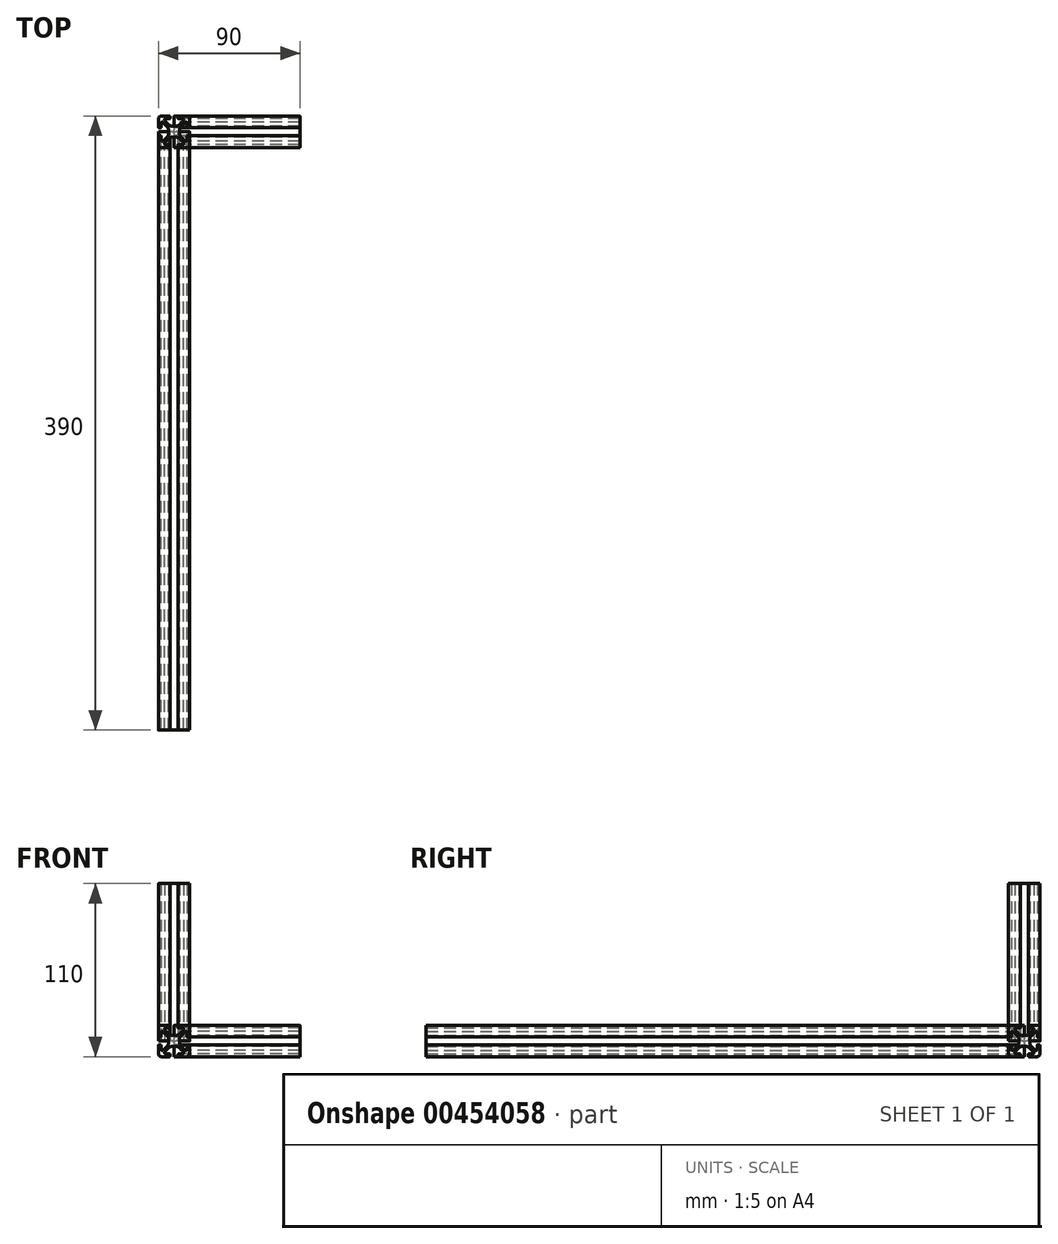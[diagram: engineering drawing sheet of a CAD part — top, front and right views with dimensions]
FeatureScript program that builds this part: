
annotation { "Feature Type Name" : "Feature", "Feature Type Description" : "" }
export const myFeature = defineFeature(function(context is Context, id is Id, definition is map)
    precondition{}
    {
        {
            var Q0;
            Q0=qCreatedBy(makeId("Top.planeOp"),FACE);
            var sketch = newSketch(context, id + "F0", { "sketchPlane" : qUnion([Q0])});
            skArc(sketch, "E0.0.0", {"start": v(-10, -8) * mm, "mid": v(-9.41, -9.41) * mm, "end": v(-8, -10) * mm});
            skLineSegment(sketch, "E0.0.1", {"start": v(-8, -10) * mm, "end": v(-3, -10) * mm});
            skArc(sketch, "E0.0.2", {"start": v(-3, -10) * mm, "mid": v(-2.65, -9.85) * mm, "end": v(-2.5, -9.5) * mm});
            skLineSegment(sketch, "E0.0.3", {"start": v(-2.5, -9.5) * mm, "end": v(-2.5, -8.4) * mm});
            skArc(sketch, "E0.0.4", {"start": v(-2.5, -8.4) * mm, "mid": v(-2.56, -8.26) * mm, "end": v(-2.7, -8.2) * mm});
            skLineSegment(sketch, "E0.0.5", {"start": v(-2.7, -8.2) * mm, "end": v(-5.34, -8.2) * mm});
            skArc(sketch, "E0.0.6", {"start": v(-5.34, -8.2) * mm, "mid": v(-6.04, -7.74) * mm, "end": v(-5.87, -6.92) * mm});
            skLineSegment(sketch, "E0.0.7", {"start": v(-5.87, -6.92) * mm, "end": v(-3.35, -4.4) * mm});
            skArc(sketch, "E0.0.8", {"start": v(-3.35, -4.4) * mm, "mid": v(-2.38, -3.75) * mm, "end": v(-1.23, -3.52) * mm});
            skLineSegment(sketch, "E0.0.9", {"start": v(-1.23, -3.52) * mm, "end": v(1.23, -3.52) * mm});
            skArc(sketch, "E0.0.10", {"start": v(1.23, -3.52) * mm, "mid": v(2.38, -3.75) * mm, "end": v(3.35, -4.4) * mm});
            skLineSegment(sketch, "E0.0.11", {"start": v(3.35, -4.4) * mm, "end": v(5.87, -6.92) * mm});
            skArc(sketch, "E0.0.12", {"start": v(5.87, -6.92) * mm, "mid": v(6.04, -7.74) * mm, "end": v(5.34, -8.2) * mm});
            skLineSegment(sketch, "E0.0.13", {"start": v(5.34, -8.2) * mm, "end": v(2.7, -8.2) * mm});
            skArc(sketch, "E0.0.14", {"start": v(2.7, -8.2) * mm, "mid": v(2.56, -8.26) * mm, "end": v(2.5, -8.4) * mm});
            skLineSegment(sketch, "E0.0.15", {"start": v(2.5, -8.4) * mm, "end": v(2.5, -9.5) * mm});
            skArc(sketch, "E0.0.16", {"start": v(2.5, -9.5) * mm, "mid": v(2.65, -9.85) * mm, "end": v(3, -10) * mm});
            skLineSegment(sketch, "E0.0.17", {"start": v(3, -10) * mm, "end": v(8, -10) * mm});
            skArc(sketch, "E0.0.18", {"start": v(8, -10) * mm, "mid": v(9.41, -9.41) * mm, "end": v(10, -8) * mm});
            skLineSegment(sketch, "E0.0.19", {"start": v(10, -8) * mm, "end": v(10, -3) * mm});
            skArc(sketch, "E0.0.20", {"start": v(10, -3) * mm, "mid": v(9.85, -2.65) * mm, "end": v(9.5, -2.5) * mm});
            skLineSegment(sketch, "E0.0.21", {"start": v(9.5, -2.5) * mm, "end": v(8.4, -2.5) * mm});
            skArc(sketch, "E0.0.22", {"start": v(8.4, -2.5) * mm, "mid": v(8.26, -2.56) * mm, "end": v(8.2, -2.7) * mm});
            skLineSegment(sketch, "E0.0.23", {"start": v(8.2, -2.7) * mm, "end": v(8.2, -5.34) * mm});
            skArc(sketch, "E0.0.24", {"start": v(8.2, -5.34) * mm, "mid": v(7.74, -6.04) * mm, "end": v(6.92, -5.87) * mm});
            skLineSegment(sketch, "E0.0.25", {"start": v(6.92, -5.87) * mm, "end": v(4.4, -3.35) * mm});
            skArc(sketch, "E0.0.26", {"start": v(4.4, -3.35) * mm, "mid": v(3.75, -2.38) * mm, "end": v(3.52, -1.23) * mm});
            skLineSegment(sketch, "E0.0.27", {"start": v(3.52, -1.23) * mm, "end": v(3.52, 1.23) * mm});
            skArc(sketch, "E0.0.28", {"start": v(3.52, 1.23) * mm, "mid": v(3.75, 2.38) * mm, "end": v(4.4, 3.35) * mm});
            skLineSegment(sketch, "E0.0.29", {"start": v(4.4, 3.35) * mm, "end": v(6.92, 5.87) * mm});
            skArc(sketch, "E0.0.30", {"start": v(6.92, 5.87) * mm, "mid": v(7.74, 6.04) * mm, "end": v(8.2, 5.34) * mm});
            skLineSegment(sketch, "E0.0.31", {"start": v(8.2, 5.34) * mm, "end": v(8.2, 2.7) * mm});
            skArc(sketch, "E0.0.32", {"start": v(8.2, 2.7) * mm, "mid": v(8.26, 2.56) * mm, "end": v(8.4, 2.5) * mm});
            skLineSegment(sketch, "E0.0.33", {"start": v(8.4, 2.5) * mm, "end": v(9.5, 2.5) * mm});
            skArc(sketch, "E0.0.34", {"start": v(9.5, 2.5) * mm, "mid": v(9.85, 2.65) * mm, "end": v(10, 3) * mm});
            skLineSegment(sketch, "E0.0.35", {"start": v(10, 3) * mm, "end": v(10, 8) * mm});
            skArc(sketch, "E0.0.36", {"start": v(10, 8) * mm, "mid": v(9.41, 9.41) * mm, "end": v(8, 10) * mm});
            skLineSegment(sketch, "E0.0.37", {"start": v(8, 10) * mm, "end": v(3, 10) * mm});
            skArc(sketch, "E0.0.38", {"start": v(3, 10) * mm, "mid": v(2.65, 9.85) * mm, "end": v(2.5, 9.5) * mm});
            skLineSegment(sketch, "E0.0.39", {"start": v(2.5, 9.5) * mm, "end": v(2.5, 8.4) * mm});
            skArc(sketch, "E0.0.40", {"start": v(2.5, 8.4) * mm, "mid": v(2.56, 8.26) * mm, "end": v(2.7, 8.2) * mm});
            skLineSegment(sketch, "E0.0.41", {"start": v(2.7, 8.2) * mm, "end": v(5.34, 8.2) * mm});
            skArc(sketch, "E0.0.42", {"start": v(5.34, 8.2) * mm, "mid": v(6.04, 7.74) * mm, "end": v(5.87, 6.92) * mm});
            skLineSegment(sketch, "E0.0.43", {"start": v(5.87, 6.92) * mm, "end": v(3.35, 4.4) * mm});
            skArc(sketch, "E0.0.44", {"start": v(3.35, 4.4) * mm, "mid": v(2.38, 3.75) * mm, "end": v(1.23, 3.52) * mm});
            skLineSegment(sketch, "E0.0.45", {"start": v(1.23, 3.52) * mm, "end": v(-1.23, 3.52) * mm});
            skArc(sketch, "E0.0.46", {"start": v(-1.23, 3.52) * mm, "mid": v(-2.38, 3.75) * mm, "end": v(-3.35, 4.4) * mm});
            skLineSegment(sketch, "E0.0.47", {"start": v(-3.35, 4.4) * mm, "end": v(-5.87, 6.92) * mm});
            skArc(sketch, "E0.0.48", {"start": v(-5.87, 6.92) * mm, "mid": v(-6.04, 7.74) * mm, "end": v(-5.34, 8.2) * mm});
            skLineSegment(sketch, "E0.0.49", {"start": v(-5.34, 8.2) * mm, "end": v(-2.7, 8.2) * mm});
            skArc(sketch, "E0.0.50", {"start": v(-2.7, 8.2) * mm, "mid": v(-2.56, 8.26) * mm, "end": v(-2.5, 8.4) * mm});
            skLineSegment(sketch, "E0.0.51", {"start": v(-2.5, 8.4) * mm, "end": v(-2.5, 9.5) * mm});
            skArc(sketch, "E0.0.52", {"start": v(-2.5, 9.5) * mm, "mid": v(-2.65, 9.85) * mm, "end": v(-3, 10) * mm});
            skLineSegment(sketch, "E0.0.53", {"start": v(-3, 10) * mm, "end": v(-8, 10) * mm});
            skArc(sketch, "E0.0.54", {"start": v(-8, 10) * mm, "mid": v(-9.41, 9.41) * mm, "end": v(-10, 8) * mm});
            skLineSegment(sketch, "E0.0.55", {"start": v(-10, 8) * mm, "end": v(-10, 3) * mm});
            skArc(sketch, "E0.0.56", {"start": v(-10, 3) * mm, "mid": v(-9.85, 2.65) * mm, "end": v(-9.5, 2.5) * mm});
            skLineSegment(sketch, "E0.0.57", {"start": v(-9.5, 2.5) * mm, "end": v(-8.4, 2.5) * mm});
            skArc(sketch, "E0.0.58", {"start": v(-8.4, 2.5) * mm, "mid": v(-8.26, 2.56) * mm, "end": v(-8.2, 2.7) * mm});
            skLineSegment(sketch, "E0.0.59", {"start": v(-8.2, 2.7) * mm, "end": v(-8.2, 5.34) * mm});
            skArc(sketch, "E0.0.60", {"start": v(-8.2, 5.34) * mm, "mid": v(-7.74, 6.04) * mm, "end": v(-6.92, 5.87) * mm});
            skLineSegment(sketch, "E0.0.61", {"start": v(-6.92, 5.87) * mm, "end": v(-4.4, 3.35) * mm});
            skArc(sketch, "E0.0.62", {"start": v(-4.4, 3.35) * mm, "mid": v(-3.75, 2.38) * mm, "end": v(-3.52, 1.23) * mm});
            skLineSegment(sketch, "E0.0.63", {"start": v(-3.52, 1.23) * mm, "end": v(-3.52, -1.23) * mm});
            skArc(sketch, "E0.0.64", {"start": v(-3.52, -1.23) * mm, "mid": v(-3.75, -2.38) * mm, "end": v(-4.4, -3.35) * mm});
            skLineSegment(sketch, "E0.0.65", {"start": v(-4.4, -3.35) * mm, "end": v(-6.92, -5.87) * mm});
            skArc(sketch, "E0.0.66", {"start": v(-6.92, -5.87) * mm, "mid": v(-7.74, -6.04) * mm, "end": v(-8.2, -5.34) * mm});
            skLineSegment(sketch, "E0.0.67", {"start": v(-8.2, -5.34) * mm, "end": v(-8.2, -2.7) * mm});
            skArc(sketch, "E0.0.68", {"start": v(-8.2, -2.7) * mm, "mid": v(-8.26, -2.56) * mm, "end": v(-8.4, -2.5) * mm});
            skLineSegment(sketch, "E0.0.69", {"start": v(-8.4, -2.5) * mm, "end": v(-9.5, -2.5) * mm});
            skArc(sketch, "E0.0.70", {"start": v(-9.5, -2.5) * mm, "mid": v(-9.85, -2.65) * mm, "end": v(-10, -3) * mm});
            skLineSegment(sketch, "E0.0.71", {"start": v(-10, -3) * mm, "end": v(-10, -8) * mm});
            skSolve(sketch);
        }
        {
            var Q0;
            Q0=qSketchRegion(id+"F0",true);
            extrude(context, id + "F1", {"entities" : qUnion([Q0]), "depth" : 100 * mm, "offsetDistance" : 25 * mm});
        }
        {
            var Q0;
            Q0=qCreatedBy(makeId("Right.planeOp"),FACE);
            var sketch = newSketch(context, id + "F2", { "sketchPlane" : qUnion([Q0])});
            skArc(sketch, "E1.0.0", {"start": v(-10, -8) * mm, "mid": v(-9.41, -9.41) * mm, "end": v(-8, -10) * mm});
            skLineSegment(sketch, "E1.0.1", {"start": v(-8, -10) * mm, "end": v(-3, -10) * mm});
            skArc(sketch, "E1.0.2", {"start": v(-3, -10) * mm, "mid": v(-2.65, -9.85) * mm, "end": v(-2.5, -9.5) * mm});
            skLineSegment(sketch, "E1.0.3", {"start": v(-2.5, -9.5) * mm, "end": v(-2.5, -8.4) * mm});
            skArc(sketch, "E1.0.4", {"start": v(-2.5, -8.4) * mm, "mid": v(-2.56, -8.26) * mm, "end": v(-2.7, -8.2) * mm});
            skLineSegment(sketch, "E1.0.5", {"start": v(-2.7, -8.2) * mm, "end": v(-5.34, -8.2) * mm});
            skArc(sketch, "E1.0.6", {"start": v(-5.34, -8.2) * mm, "mid": v(-6.04, -7.74) * mm, "end": v(-5.87, -6.92) * mm});
            skLineSegment(sketch, "E1.0.7", {"start": v(-5.87, -6.92) * mm, "end": v(-3.35, -4.4) * mm});
            skArc(sketch, "E1.0.8", {"start": v(-3.35, -4.4) * mm, "mid": v(-2.38, -3.75) * mm, "end": v(-1.23, -3.52) * mm});
            skLineSegment(sketch, "E1.0.9", {"start": v(-1.23, -3.52) * mm, "end": v(1.23, -3.52) * mm});
            skArc(sketch, "E1.0.10", {"start": v(1.23, -3.52) * mm, "mid": v(2.38, -3.75) * mm, "end": v(3.35, -4.4) * mm});
            skLineSegment(sketch, "E1.0.11", {"start": v(3.35, -4.4) * mm, "end": v(5.87, -6.92) * mm});
            skArc(sketch, "E1.0.12", {"start": v(5.87, -6.92) * mm, "mid": v(6.04, -7.74) * mm, "end": v(5.34, -8.2) * mm});
            skLineSegment(sketch, "E1.0.13", {"start": v(5.34, -8.2) * mm, "end": v(2.7, -8.2) * mm});
            skArc(sketch, "E1.0.14", {"start": v(2.7, -8.2) * mm, "mid": v(2.56, -8.26) * mm, "end": v(2.5, -8.4) * mm});
            skLineSegment(sketch, "E1.0.15", {"start": v(2.5, -8.4) * mm, "end": v(2.5, -9.5) * mm});
            skArc(sketch, "E1.0.16", {"start": v(2.5, -9.5) * mm, "mid": v(2.65, -9.85) * mm, "end": v(3, -10) * mm});
            skLineSegment(sketch, "E1.0.17", {"start": v(3, -10) * mm, "end": v(8, -10) * mm});
            skArc(sketch, "E1.0.18", {"start": v(8, -10) * mm, "mid": v(9.41, -9.41) * mm, "end": v(10, -8) * mm});
            skLineSegment(sketch, "E1.0.19", {"start": v(10, -8) * mm, "end": v(10, -3) * mm});
            skArc(sketch, "E1.0.20", {"start": v(10, -3) * mm, "mid": v(9.85, -2.65) * mm, "end": v(9.5, -2.5) * mm});
            skLineSegment(sketch, "E1.0.21", {"start": v(9.5, -2.5) * mm, "end": v(8.4, -2.5) * mm});
            skArc(sketch, "E1.0.22", {"start": v(8.4, -2.5) * mm, "mid": v(8.26, -2.56) * mm, "end": v(8.2, -2.7) * mm});
            skLineSegment(sketch, "E1.0.23", {"start": v(8.2, -2.7) * mm, "end": v(8.2, -5.34) * mm});
            skArc(sketch, "E1.0.24", {"start": v(8.2, -5.34) * mm, "mid": v(7.74, -6.04) * mm, "end": v(6.92, -5.87) * mm});
            skLineSegment(sketch, "E1.0.25", {"start": v(6.92, -5.87) * mm, "end": v(4.4, -3.35) * mm});
            skArc(sketch, "E1.0.26", {"start": v(4.4, -3.35) * mm, "mid": v(3.75, -2.38) * mm, "end": v(3.52, -1.23) * mm});
            skLineSegment(sketch, "E1.0.27", {"start": v(3.52, -1.23) * mm, "end": v(3.52, 1.23) * mm});
            skArc(sketch, "E1.0.28", {"start": v(3.52, 1.23) * mm, "mid": v(3.75, 2.38) * mm, "end": v(4.4, 3.35) * mm});
            skLineSegment(sketch, "E1.0.29", {"start": v(4.4, 3.35) * mm, "end": v(6.92, 5.87) * mm});
            skArc(sketch, "E1.0.30", {"start": v(6.92, 5.87) * mm, "mid": v(7.74, 6.04) * mm, "end": v(8.2, 5.34) * mm});
            skLineSegment(sketch, "E1.0.31", {"start": v(8.2, 5.34) * mm, "end": v(8.2, 2.7) * mm});
            skArc(sketch, "E1.0.32", {"start": v(8.2, 2.7) * mm, "mid": v(8.26, 2.56) * mm, "end": v(8.4, 2.5) * mm});
            skLineSegment(sketch, "E1.0.33", {"start": v(8.4, 2.5) * mm, "end": v(9.5, 2.5) * mm});
            skArc(sketch, "E1.0.34", {"start": v(9.5, 2.5) * mm, "mid": v(9.85, 2.65) * mm, "end": v(10, 3) * mm});
            skLineSegment(sketch, "E1.0.35", {"start": v(10, 3) * mm, "end": v(10, 8) * mm});
            skArc(sketch, "E1.0.36", {"start": v(10, 8) * mm, "mid": v(9.41, 9.41) * mm, "end": v(8, 10) * mm});
            skLineSegment(sketch, "E1.0.37", {"start": v(8, 10) * mm, "end": v(3, 10) * mm});
            skArc(sketch, "E1.0.38", {"start": v(3, 10) * mm, "mid": v(2.65, 9.85) * mm, "end": v(2.5, 9.5) * mm});
            skLineSegment(sketch, "E1.0.39", {"start": v(2.5, 9.5) * mm, "end": v(2.5, 8.4) * mm});
            skArc(sketch, "E1.0.40", {"start": v(2.5, 8.4) * mm, "mid": v(2.56, 8.26) * mm, "end": v(2.7, 8.2) * mm});
            skLineSegment(sketch, "E1.0.41", {"start": v(2.7, 8.2) * mm, "end": v(5.34, 8.2) * mm});
            skArc(sketch, "E1.0.42", {"start": v(5.34, 8.2) * mm, "mid": v(6.04, 7.74) * mm, "end": v(5.87, 6.92) * mm});
            skLineSegment(sketch, "E1.0.43", {"start": v(5.87, 6.92) * mm, "end": v(3.35, 4.4) * mm});
            skArc(sketch, "E1.0.44", {"start": v(3.35, 4.4) * mm, "mid": v(2.38, 3.75) * mm, "end": v(1.23, 3.52) * mm});
            skLineSegment(sketch, "E1.0.45", {"start": v(1.23, 3.52) * mm, "end": v(-1.23, 3.52) * mm});
            skArc(sketch, "E1.0.46", {"start": v(-1.23, 3.52) * mm, "mid": v(-2.38, 3.75) * mm, "end": v(-3.35, 4.4) * mm});
            skLineSegment(sketch, "E1.0.47", {"start": v(-3.35, 4.4) * mm, "end": v(-5.87, 6.92) * mm});
            skArc(sketch, "E1.0.48", {"start": v(-5.87, 6.92) * mm, "mid": v(-6.04, 7.74) * mm, "end": v(-5.34, 8.2) * mm});
            skLineSegment(sketch, "E1.0.49", {"start": v(-5.34, 8.2) * mm, "end": v(-2.7, 8.2) * mm});
            skArc(sketch, "E1.0.50", {"start": v(-2.7, 8.2) * mm, "mid": v(-2.56, 8.26) * mm, "end": v(-2.5, 8.4) * mm});
            skLineSegment(sketch, "E1.0.51", {"start": v(-2.5, 8.4) * mm, "end": v(-2.5, 9.5) * mm});
            skArc(sketch, "E1.0.52", {"start": v(-2.5, 9.5) * mm, "mid": v(-2.65, 9.85) * mm, "end": v(-3, 10) * mm});
            skLineSegment(sketch, "E1.0.53", {"start": v(-3, 10) * mm, "end": v(-8, 10) * mm});
            skArc(sketch, "E1.0.54", {"start": v(-8, 10) * mm, "mid": v(-9.41, 9.41) * mm, "end": v(-10, 8) * mm});
            skLineSegment(sketch, "E1.0.55", {"start": v(-10, 8) * mm, "end": v(-10, 3) * mm});
            skArc(sketch, "E1.0.56", {"start": v(-10, 3) * mm, "mid": v(-9.85, 2.65) * mm, "end": v(-9.5, 2.5) * mm});
            skLineSegment(sketch, "E1.0.57", {"start": v(-9.5, 2.5) * mm, "end": v(-8.4, 2.5) * mm});
            skArc(sketch, "E1.0.58", {"start": v(-8.4, 2.5) * mm, "mid": v(-8.26, 2.56) * mm, "end": v(-8.2, 2.7) * mm});
            skLineSegment(sketch, "E1.0.59", {"start": v(-8.2, 2.7) * mm, "end": v(-8.2, 5.34) * mm});
            skArc(sketch, "E1.0.60", {"start": v(-8.2, 5.34) * mm, "mid": v(-7.74, 6.04) * mm, "end": v(-6.92, 5.87) * mm});
            skLineSegment(sketch, "E1.0.61", {"start": v(-6.92, 5.87) * mm, "end": v(-4.4, 3.35) * mm});
            skArc(sketch, "E1.0.62", {"start": v(-4.4, 3.35) * mm, "mid": v(-3.75, 2.38) * mm, "end": v(-3.52, 1.23) * mm});
            skLineSegment(sketch, "E1.0.63", {"start": v(-3.52, 1.23) * mm, "end": v(-3.52, -1.23) * mm});
            skArc(sketch, "E1.0.64", {"start": v(-3.52, -1.23) * mm, "mid": v(-3.75, -2.38) * mm, "end": v(-4.4, -3.35) * mm});
            skLineSegment(sketch, "E1.0.65", {"start": v(-4.4, -3.35) * mm, "end": v(-6.92, -5.87) * mm});
            skArc(sketch, "E1.0.66", {"start": v(-6.92, -5.87) * mm, "mid": v(-7.74, -6.04) * mm, "end": v(-8.2, -5.34) * mm});
            skLineSegment(sketch, "E1.0.67", {"start": v(-8.2, -5.34) * mm, "end": v(-8.2, -2.7) * mm});
            skArc(sketch, "E1.0.68", {"start": v(-8.2, -2.7) * mm, "mid": v(-8.26, -2.56) * mm, "end": v(-8.4, -2.5) * mm});
            skLineSegment(sketch, "E1.0.69", {"start": v(-8.4, -2.5) * mm, "end": v(-9.5, -2.5) * mm});
            skArc(sketch, "E1.0.70", {"start": v(-9.5, -2.5) * mm, "mid": v(-9.85, -2.65) * mm, "end": v(-10, -3) * mm});
            skLineSegment(sketch, "E1.0.71", {"start": v(-10, -3) * mm, "end": v(-10, -8) * mm});
            skSolve(sketch);
        }
        {
            var Q0;
            Q0=qSketchRegion(id+"F2",true);
            extrude(context, id + "F3", {"entities" : qUnion([Q0]), "depth" : 80 * mm, "offsetDistance" : 25 * mm});
        }
        {
            var Q0;
            Q0=qCreatedBy(makeId("Front.planeOp"),FACE);
            var sketch = newSketch(context, id + "F4", { "sketchPlane" : qUnion([Q0])});
            skArc(sketch, "E2.0.0", {"start": v(-10, -8) * mm, "mid": v(-9.41, -9.41) * mm, "end": v(-8, -10) * mm});
            skLineSegment(sketch, "E2.0.1", {"start": v(-8, -10) * mm, "end": v(-3, -10) * mm});
            skArc(sketch, "E2.0.2", {"start": v(-3, -10) * mm, "mid": v(-2.65, -9.85) * mm, "end": v(-2.5, -9.5) * mm});
            skLineSegment(sketch, "E2.0.3", {"start": v(-2.5, -9.5) * mm, "end": v(-2.5, -8.4) * mm});
            skArc(sketch, "E2.0.4", {"start": v(-2.5, -8.4) * mm, "mid": v(-2.56, -8.26) * mm, "end": v(-2.7, -8.2) * mm});
            skLineSegment(sketch, "E2.0.5", {"start": v(-2.7, -8.2) * mm, "end": v(-5.34, -8.2) * mm});
            skArc(sketch, "E2.0.6", {"start": v(-5.34, -8.2) * mm, "mid": v(-6.04, -7.74) * mm, "end": v(-5.87, -6.92) * mm});
            skLineSegment(sketch, "E2.0.7", {"start": v(-5.87, -6.92) * mm, "end": v(-3.35, -4.4) * mm});
            skArc(sketch, "E2.0.8", {"start": v(-3.35, -4.4) * mm, "mid": v(-2.38, -3.75) * mm, "end": v(-1.23, -3.52) * mm});
            skLineSegment(sketch, "E2.0.9", {"start": v(-1.23, -3.52) * mm, "end": v(1.23, -3.52) * mm});
            skArc(sketch, "E2.0.10", {"start": v(1.23, -3.52) * mm, "mid": v(2.38, -3.75) * mm, "end": v(3.35, -4.4) * mm});
            skLineSegment(sketch, "E2.0.11", {"start": v(3.35, -4.4) * mm, "end": v(5.87, -6.92) * mm});
            skArc(sketch, "E2.0.12", {"start": v(5.87, -6.92) * mm, "mid": v(6.04, -7.74) * mm, "end": v(5.34, -8.2) * mm});
            skLineSegment(sketch, "E2.0.13", {"start": v(5.34, -8.2) * mm, "end": v(2.7, -8.2) * mm});
            skArc(sketch, "E2.0.14", {"start": v(2.7, -8.2) * mm, "mid": v(2.56, -8.26) * mm, "end": v(2.5, -8.4) * mm});
            skLineSegment(sketch, "E2.0.15", {"start": v(2.5, -8.4) * mm, "end": v(2.5, -9.5) * mm});
            skArc(sketch, "E2.0.16", {"start": v(2.5, -9.5) * mm, "mid": v(2.65, -9.85) * mm, "end": v(3, -10) * mm});
            skLineSegment(sketch, "E2.0.17", {"start": v(3, -10) * mm, "end": v(8, -10) * mm});
            skArc(sketch, "E2.0.18", {"start": v(8, -10) * mm, "mid": v(9.41, -9.41) * mm, "end": v(10, -8) * mm});
            skLineSegment(sketch, "E2.0.19", {"start": v(10, -8) * mm, "end": v(10, -3) * mm});
            skArc(sketch, "E2.0.20", {"start": v(10, -3) * mm, "mid": v(9.85, -2.65) * mm, "end": v(9.5, -2.5) * mm});
            skLineSegment(sketch, "E2.0.21", {"start": v(9.5, -2.5) * mm, "end": v(8.4, -2.5) * mm});
            skArc(sketch, "E2.0.22", {"start": v(8.4, -2.5) * mm, "mid": v(8.26, -2.56) * mm, "end": v(8.2, -2.7) * mm});
            skLineSegment(sketch, "E2.0.23", {"start": v(8.2, -2.7) * mm, "end": v(8.2, -5.34) * mm});
            skArc(sketch, "E2.0.24", {"start": v(8.2, -5.34) * mm, "mid": v(7.74, -6.04) * mm, "end": v(6.92, -5.87) * mm});
            skLineSegment(sketch, "E2.0.25", {"start": v(6.92, -5.87) * mm, "end": v(4.4, -3.35) * mm});
            skArc(sketch, "E2.0.26", {"start": v(4.4, -3.35) * mm, "mid": v(3.75, -2.38) * mm, "end": v(3.52, -1.23) * mm});
            skLineSegment(sketch, "E2.0.27", {"start": v(3.52, -1.23) * mm, "end": v(3.52, 1.23) * mm});
            skArc(sketch, "E2.0.28", {"start": v(3.52, 1.23) * mm, "mid": v(3.75, 2.38) * mm, "end": v(4.4, 3.35) * mm});
            skLineSegment(sketch, "E2.0.29", {"start": v(4.4, 3.35) * mm, "end": v(6.92, 5.87) * mm});
            skArc(sketch, "E2.0.30", {"start": v(6.92, 5.87) * mm, "mid": v(7.74, 6.04) * mm, "end": v(8.2, 5.34) * mm});
            skLineSegment(sketch, "E2.0.31", {"start": v(8.2, 5.34) * mm, "end": v(8.2, 2.7) * mm});
            skArc(sketch, "E2.0.32", {"start": v(8.2, 2.7) * mm, "mid": v(8.26, 2.56) * mm, "end": v(8.4, 2.5) * mm});
            skLineSegment(sketch, "E2.0.33", {"start": v(8.4, 2.5) * mm, "end": v(9.5, 2.5) * mm});
            skArc(sketch, "E2.0.34", {"start": v(9.5, 2.5) * mm, "mid": v(9.85, 2.65) * mm, "end": v(10, 3) * mm});
            skLineSegment(sketch, "E2.0.35", {"start": v(10, 3) * mm, "end": v(10, 8) * mm});
            skArc(sketch, "E2.0.36", {"start": v(10, 8) * mm, "mid": v(9.41, 9.41) * mm, "end": v(8, 10) * mm});
            skLineSegment(sketch, "E2.0.37", {"start": v(8, 10) * mm, "end": v(3, 10) * mm});
            skArc(sketch, "E2.0.38", {"start": v(3, 10) * mm, "mid": v(2.65, 9.85) * mm, "end": v(2.5, 9.5) * mm});
            skLineSegment(sketch, "E2.0.39", {"start": v(2.5, 9.5) * mm, "end": v(2.5, 8.4) * mm});
            skArc(sketch, "E2.0.40", {"start": v(2.5, 8.4) * mm, "mid": v(2.56, 8.26) * mm, "end": v(2.7, 8.2) * mm});
            skLineSegment(sketch, "E2.0.41", {"start": v(2.7, 8.2) * mm, "end": v(5.34, 8.2) * mm});
            skArc(sketch, "E2.0.42", {"start": v(5.34, 8.2) * mm, "mid": v(6.04, 7.74) * mm, "end": v(5.87, 6.92) * mm});
            skLineSegment(sketch, "E2.0.43", {"start": v(5.87, 6.92) * mm, "end": v(3.35, 4.4) * mm});
            skArc(sketch, "E2.0.44", {"start": v(3.35, 4.4) * mm, "mid": v(2.38, 3.75) * mm, "end": v(1.23, 3.52) * mm});
            skLineSegment(sketch, "E2.0.45", {"start": v(1.23, 3.52) * mm, "end": v(-1.23, 3.52) * mm});
            skArc(sketch, "E2.0.46", {"start": v(-1.23, 3.52) * mm, "mid": v(-2.38, 3.75) * mm, "end": v(-3.35, 4.4) * mm});
            skLineSegment(sketch, "E2.0.47", {"start": v(-3.35, 4.4) * mm, "end": v(-5.87, 6.92) * mm});
            skArc(sketch, "E2.0.48", {"start": v(-5.87, 6.92) * mm, "mid": v(-6.04, 7.74) * mm, "end": v(-5.34, 8.2) * mm});
            skLineSegment(sketch, "E2.0.49", {"start": v(-5.34, 8.2) * mm, "end": v(-2.7, 8.2) * mm});
            skArc(sketch, "E2.0.50", {"start": v(-2.7, 8.2) * mm, "mid": v(-2.56, 8.26) * mm, "end": v(-2.5, 8.4) * mm});
            skLineSegment(sketch, "E2.0.51", {"start": v(-2.5, 8.4) * mm, "end": v(-2.5, 9.5) * mm});
            skArc(sketch, "E2.0.52", {"start": v(-2.5, 9.5) * mm, "mid": v(-2.65, 9.85) * mm, "end": v(-3, 10) * mm});
            skLineSegment(sketch, "E2.0.53", {"start": v(-3, 10) * mm, "end": v(-8, 10) * mm});
            skArc(sketch, "E2.0.54", {"start": v(-8, 10) * mm, "mid": v(-9.41, 9.41) * mm, "end": v(-10, 8) * mm});
            skLineSegment(sketch, "E2.0.55", {"start": v(-10, 8) * mm, "end": v(-10, 3) * mm});
            skArc(sketch, "E2.0.56", {"start": v(-10, 3) * mm, "mid": v(-9.85, 2.65) * mm, "end": v(-9.5, 2.5) * mm});
            skLineSegment(sketch, "E2.0.57", {"start": v(-9.5, 2.5) * mm, "end": v(-8.4, 2.5) * mm});
            skArc(sketch, "E2.0.58", {"start": v(-8.4, 2.5) * mm, "mid": v(-8.26, 2.56) * mm, "end": v(-8.2, 2.7) * mm});
            skLineSegment(sketch, "E2.0.59", {"start": v(-8.2, 2.7) * mm, "end": v(-8.2, 5.34) * mm});
            skArc(sketch, "E2.0.60", {"start": v(-8.2, 5.34) * mm, "mid": v(-7.74, 6.04) * mm, "end": v(-6.92, 5.87) * mm});
            skLineSegment(sketch, "E2.0.61", {"start": v(-6.92, 5.87) * mm, "end": v(-4.4, 3.35) * mm});
            skArc(sketch, "E2.0.62", {"start": v(-4.4, 3.35) * mm, "mid": v(-3.75, 2.38) * mm, "end": v(-3.52, 1.23) * mm});
            skLineSegment(sketch, "E2.0.63", {"start": v(-3.52, 1.23) * mm, "end": v(-3.52, -1.23) * mm});
            skArc(sketch, "E2.0.64", {"start": v(-3.52, -1.23) * mm, "mid": v(-3.75, -2.38) * mm, "end": v(-4.4, -3.35) * mm});
            skLineSegment(sketch, "E2.0.65", {"start": v(-4.4, -3.35) * mm, "end": v(-6.92, -5.87) * mm});
            skArc(sketch, "E2.0.66", {"start": v(-6.92, -5.87) * mm, "mid": v(-7.74, -6.04) * mm, "end": v(-8.2, -5.34) * mm});
            skLineSegment(sketch, "E2.0.67", {"start": v(-8.2, -5.34) * mm, "end": v(-8.2, -2.7) * mm});
            skArc(sketch, "E2.0.68", {"start": v(-8.2, -2.7) * mm, "mid": v(-8.26, -2.56) * mm, "end": v(-8.4, -2.5) * mm});
            skLineSegment(sketch, "E2.0.69", {"start": v(-8.4, -2.5) * mm, "end": v(-9.5, -2.5) * mm});
            skArc(sketch, "E2.0.70", {"start": v(-9.5, -2.5) * mm, "mid": v(-9.85, -2.65) * mm, "end": v(-10, -3) * mm});
            skLineSegment(sketch, "E2.0.71", {"start": v(-10, -3) * mm, "end": v(-10, -8) * mm});
            skSolve(sketch);
        }
        {
            var Q0;
            Q0=qSketchRegion(id+"F4",true);
            extrude(context, id + "F5", {"entities" : qUnion([Q0]), "depth" : 380 * mm, "offsetDistance" : 25 * mm});
        }
    });
